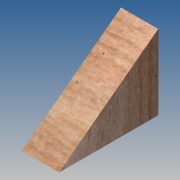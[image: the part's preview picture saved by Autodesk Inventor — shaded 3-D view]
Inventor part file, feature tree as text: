
AUTODESK INVENTOR PART (.ipt)
format: ipt  version: 2014 SP1 (Build 180222100, 222)  size: 99,328 bytes
history: native  units: in
note: dims shown in document units (in); Inventor stores cm internally (conversion verified against a paired STEP export)
features: extrude x1, sketch x1
ambient origin geometry x8: Origin, YZ Plane, XZ Plane, XY Plane, X Axis, Y Axis, Z Axis, Center Point
bodies: Solid1 (feature_tree)
feature tree (2):
  extrude  "Extrusion1"  Depth=1.5in
  sketch  "Sketch1"  dims[d0=5.0in d1=0.3642in d2=1.5in d3=0.0in]
